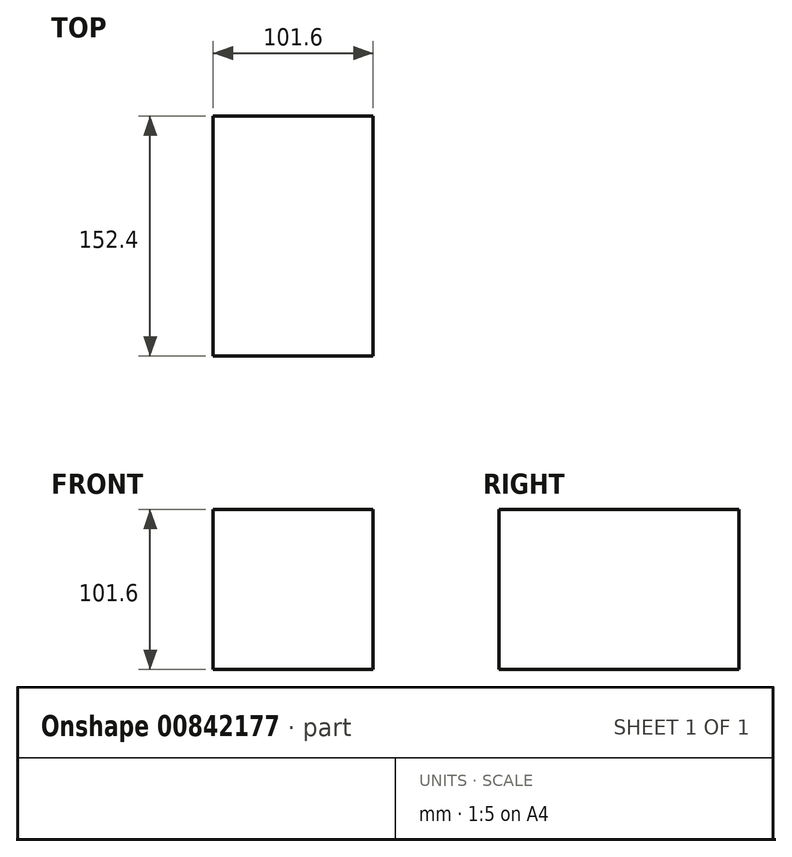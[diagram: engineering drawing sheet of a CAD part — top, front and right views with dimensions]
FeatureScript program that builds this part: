
annotation { "Feature Type Name" : "Feature", "Feature Type Description" : "" }
export const myFeature = defineFeature(function(context is Context, id is Id, definition is map)
    precondition{}
    {
        {
            var Q0;
            Q0=qCreatedBy(makeId("Top.planeOp"),FACE);
            var sketch = newSketch(context, id + "F0", { "sketchPlane" : qUnion([Q0])});
            skLineSegment(sketch, "E0.bottom", {"start": v(-40.84, 72.8) * mm, "end": v(60.76, 72.8) * mm});
            skLineSegment(sketch, "E0.top", {"start": v(-40.84, -79.6) * mm, "end": v(60.76, -79.6) * mm});
            skLineSegment(sketch, "E0.left", {"start": v(-40.84, 72.8) * mm, "end": v(-40.84, -79.6) * mm});
            skLineSegment(sketch, "E0.right", {"start": v(60.76, 72.8) * mm, "end": v(60.76, -79.6) * mm});
            skSolve(sketch);
        }
        {
            var Q0;
            Q0=makeQuery(id+"F0.imprint","IMPRINT",FACE,{"disambiguationData":[TD([[makeQuery(id+"F0.imprint","IMPRINT",EDGE,{"derivedFrom":sQuery(id+"F0.wireOp",EDGE,"E0.bottom")}),-1.0]])]});
            extrude(context, id + "F1", {"entities" : qUnion([Q0]), "depth" : 101.6 * mm, "offsetDistance" : 25.4 * mm});
        }
    });
